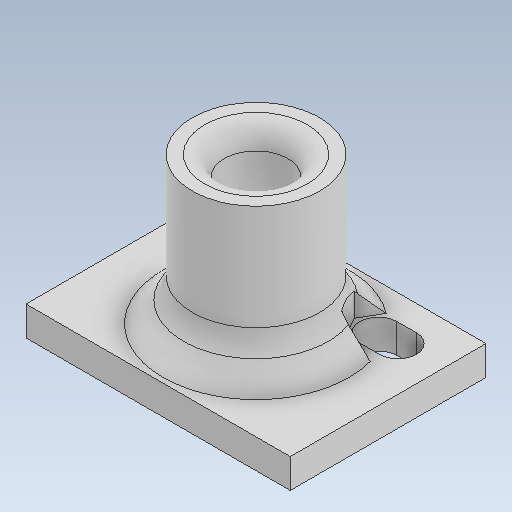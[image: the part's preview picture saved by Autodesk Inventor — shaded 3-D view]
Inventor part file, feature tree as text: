
AUTODESK INVENTOR PART (.ipt)
format: ipt  version: 2020.2 (Build 242310000, 310)  size: 254,464 bytes
history: native  units: mm
features: extrude x4, sketch x3, fillet x2, chamfer x1
ambient origin geometry x8: Origin, YZ Plane, XZ Plane, XY Plane, X Axis, Y Axis, Z Axis, Center Point
bodies: Solido1 (feature_tree)
feature tree (10):
  extrude  "Estrusione1"  Depth=6.5mm
  extrude  "Estrusione2"  Depth=13.0mm
  extrude  "Estrusione3"  Depth=15.0mm TaperAngle=0.0deg
  fillet  "Raccordo2"  Radius=20.0mm
  chamfer  "Smusso2"  Distance=27.0mm
  fillet  "Raccordo3"  Radius=3.0mm
  extrude  "Estrusione6"  Depth=8.0mm
  sketch  "Schizzo1"
  sketch  "Schizzo2"
  sketch  "Schizzo4"
